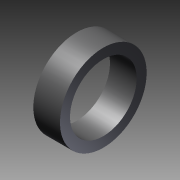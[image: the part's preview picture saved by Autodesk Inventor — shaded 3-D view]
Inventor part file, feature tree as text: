
AUTODESK INVENTOR PART (.ipt)
format: ipt  version: 2016 (Build 200138000, 138)  size: 96,256 bytes
history: native  units: mm
features: other x7, revolve x1, sketch x1
ambient origin geometry x8: Origin, YZ Plane, XZ Plane, XY Plane, X Axis, Y Axis, Z Axis, Center Point
bodies: Solid1 (feature_tree)
feature tree (9):
  revolve  "Revolution1"  [1 undecoded]
  other  "collar_XY"
  other  "collar_YZ"
  other  "collar_ZX"
  other  "collar_X"
  other  "collar_Y"
  other  "collar_Z"
  other  "collar_Center"
  sketch  "Sketch_1"  dims[d0=360.0deg d1=0.0mm]
note: 1 required parameter value undecoded (feature->parameter linkage not recoverable at this tier; creation-order binding heuristic only, values carry confidence <= 0.55)
